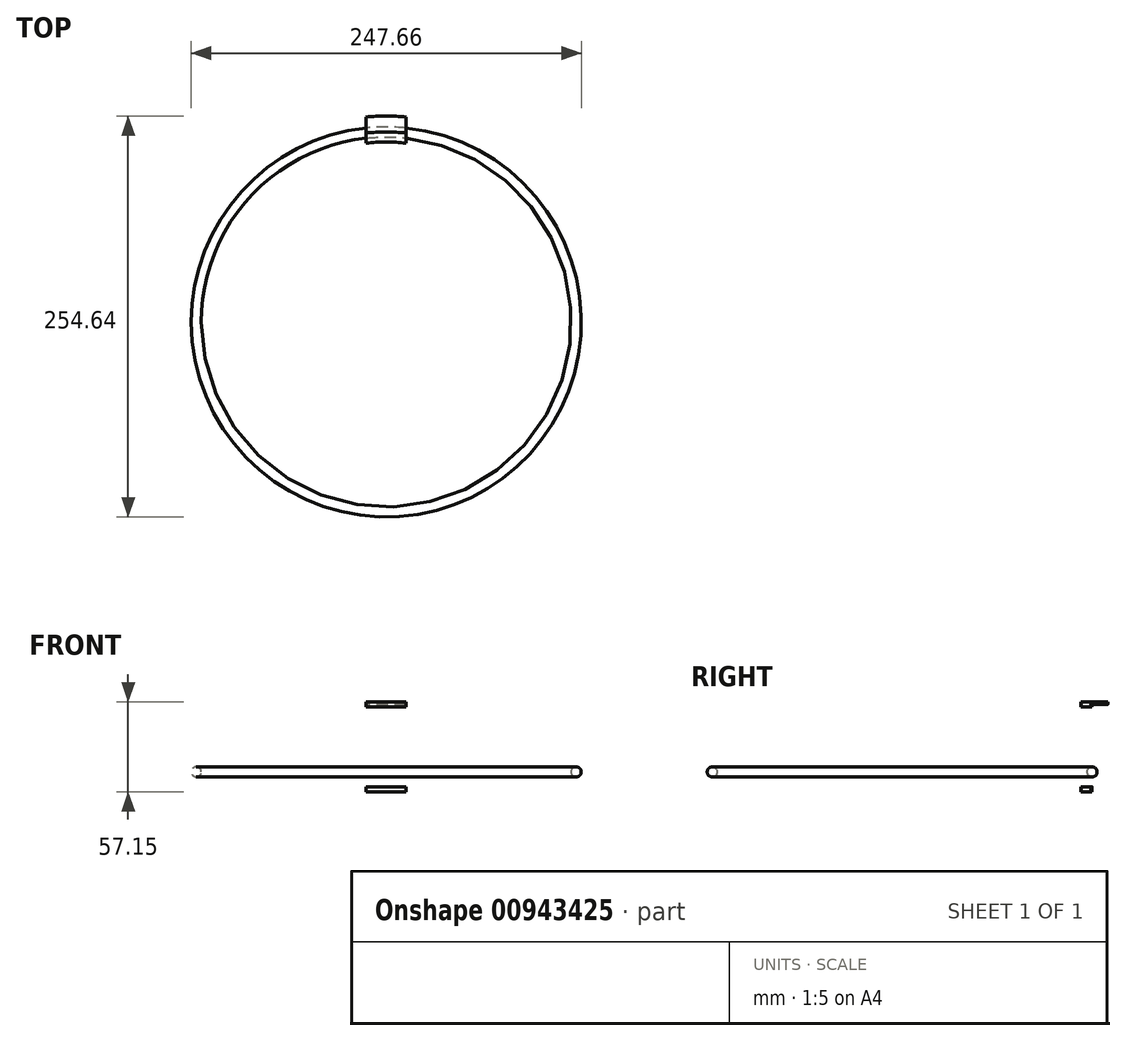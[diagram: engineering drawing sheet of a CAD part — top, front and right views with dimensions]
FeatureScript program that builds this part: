
annotation { "Feature Type Name" : "Feature", "Feature Type Description" : "" }
export const myFeature = defineFeature(function(context is Context, id is Id, definition is map)
    precondition{}
    {
        {
            var Q0;
            Q0=qCreatedBy(makeId("Right.planeOp"),FACE);
            var sketch = newSketch(context, id + "F0", { "sketchPlane" : qUnion([Q0])});
            skLineSegment(sketch, "E0", {"start": v(0, -83.04) * mm, "end": v(0, 246.82) * mm});
            skLineSegment(sketch, "E1", {"start": v(-114.3, 0) * mm, "end": v(-114.3, 57.15) * mm});
            skLineSegment(sketch, "E2", {"start": v(-114.3, 57.15) * mm, "end": v(-120.65, 57.15) * mm});
            skLineSegment(sketch, "E3", {"start": v(-120.65, 57.15) * mm, "end": v(-120.65, 0) * mm});
            skLineSegment(sketch, "E4", {"start": v(-120.65, 0) * mm, "end": v(-114.3, 0) * mm});
            skCircle(sketch, "E5", {"center": v(-120.65, 44.45) * mm, "radius": 3.18 * mm});
            skCircle(sketch, "E6", {"center": v(-120.65, 12.7) * mm, "radius": 3.18 * mm});
            skLineSegment(sketch, "E7.top", {"start": v(-114.3, 53.98) * mm, "end": v(-120.65, 53.98) * mm});
            skLineSegment(sketch, "E7.left", {"start": v(-114.3, 57.15) * mm, "end": v(-114.3, 53.98) * mm});
            skLineSegment(sketch, "E7.right", {"start": v(-120.65, 57.15) * mm, "end": v(-120.65, 53.98) * mm});
            skLineSegment(sketch, "E8.bottom", {"start": v(-114.3, 0) * mm, "end": v(-120.65, 0) * mm});
            skLineSegment(sketch, "E8.top", {"start": v(-114.3, 3.18) * mm, "end": v(-120.65, 3.18) * mm});
            skLineSegment(sketch, "E8.left", {"start": v(-114.3, 0) * mm, "end": v(-114.3, 3.18) * mm});
            skLineSegment(sketch, "E8.right", {"start": v(-120.65, 0) * mm, "end": v(-120.65, 3.18) * mm});
            skSolve(sketch);
        }
        {
            var Q0;
            Q0=makeQuery(id+"F0.imprint","IMPRINT",FACE,{"disambiguationData":[TD([[makeQuery(id+"F0.imprint","IMPRINT",EDGE,{"derivedFrom":sQuery(id+"F0.wireOp",EDGE,"E1")}),1.0]])]});
            var Q1;
            Q1=sQuery(id+"F0.wireOp",EDGE,"E0");
            revolve(context, id + "F1", {"surfaceOperationType" : NewSurfaceOperationType.NEW, "entities" : qUnion([Q0]), "axis" : qUnion([Q1]), "revolveType" : RevolveType.FULL});
        }
        {
            var Q0;
            Q0=qCreatedBy(makeId("Right.planeOp"),FACE);
            var sketch = newSketch(context, id + "F2", { "sketchPlane" : qUnion([Q0])});
            skLineSegment(sketch, "E9", {"start": v(0, 37.9) * mm, "end": v(0, -20.13) * mm});
            skLineSegment(sketch, "E10", {"start": v(120.65, 0) * mm, "end": v(120.65, 57.15) * mm});
            skLineSegment(sketch, "E11", {"start": v(120.65, 57.15) * mm, "end": v(130.8, 57.15) * mm});
            skLineSegment(sketch, "E12", {"start": v(130.8, 57.15) * mm, "end": v(130.8, 0) * mm});
            skLineSegment(sketch, "E13", {"start": v(130.8, 0) * mm, "end": v(120.65, 0) * mm});
            skCircle(sketch, "E14", {"center": v(120.65, 44.45) * mm, "radius": 3.18 * mm});
            skCircle(sketch, "E15", {"center": v(120.65, 12.7) * mm, "radius": 3.18 * mm});
            skLineSegment(sketch, "E16.top", {"start": v(120.65, 55.56) * mm, "end": v(130.8, 55.56) * mm});
            skLineSegment(sketch, "E16.left", {"start": v(120.65, 57.15) * mm, "end": v(120.65, 55.56) * mm});
            skLineSegment(sketch, "E16.right", {"start": v(130.8, 57.15) * mm, "end": v(130.8, 55.56) * mm});
            skSolve(sketch);
        }
        {
            var Q0;
            Q0=makeQuery(id+"F2.imprint","IMPRINT",FACE,{"disambiguationData":[TD([[makeQuery(id+"F2.imprint","IMPRINT",EDGE,{"derivedFrom":sQuery(id+"F2.wireOp",EDGE,"E12")}),-1.0]])]});
            var Q1;
            Q1=sQuery(id+"F2.wireOp",EDGE,"E9");
            revolve(context, id + "F3", {"surfaceOperationType" : NewSurfaceOperationType.NEW, "entities" : qUnion([Q0]), "axis" : qUnion([Q1]), "revolveType" : RevolveType.FULL});
        }
        {
            var Q0;
            Q0=qCreatedBy(makeId("Front.planeOp"),FACE);
            var sketch = newSketch(context, id + "F4", { "sketchPlane" : qUnion([Q0])});
            skLineSegment(sketch, "E17.bottom", {"start": v(12.7, 0) * mm, "end": v(-12.7, 0) * mm});
            skLineSegment(sketch, "E17.top", {"start": v(12.7, 76.2) * mm, "end": v(-12.7, 76.2) * mm});
            skLineSegment(sketch, "E17.left", {"start": v(12.7, 0) * mm, "end": v(12.7, 76.2) * mm});
            skLineSegment(sketch, "E17.right", {"start": v(-12.7, 0) * mm, "end": v(-12.7, 76.2) * mm});
            skPoint(sketch, "E18", {"position": v(0, 0) * mm});
            skSolve(sketch);
        }
        {
            var Q0;
            Q0=makeQuery(id+"F0.imprint","IMPRINT",FACE,{"disambiguationData":[TD([[makeQuery(id+"F0.imprint","IMPRINT",EDGE,{"derivedFrom":sQuery(id+"F0.wireOp",EDGE,"E1")}),1.0]])]});
            var Q1;
            Q1=sQuery(id+"F0.wireOp",EDGE,"E0");
            revolve(context, id + "F5", {"surfaceOperationType" : NewSurfaceOperationType.NEW, "entities" : qUnion([Q0]), "axis" : qUnion([Q1]), "revolveType" : RevolveType.FULL});
        }
        {
            var Q0;
            Q0 = qSketchRegion(id + "F4", true);
            extrude(context, id + "F6", {"entities" : qUnion([Q0]), "operationType" : NewBodyOperationType.INTERSECT, "endBound" : BoundingType.THROUGH_ALL, "oppositeDirection" : true, "depth" : 25.4 * mm, "offsetDistance" : 25.4 * mm});
        }
        {
            var Q0;
            Q0=qCreatedBy(makeId("Front.planeOp"),FACE);
            var sketch = newSketch(context, id + "F7", { "sketchPlane" : qUnion([Q0])});
            skLineSegment(sketch, "E19.bottom", {"start": v(-25.4, 22.23) * mm, "end": v(25.4, 22.23) * mm});
            skLineSegment(sketch, "E19.top", {"start": v(-25.4, 34.93) * mm, "end": v(25.4, 34.93) * mm});
            skLineSegment(sketch, "E19.left", {"start": v(-25.4, 22.23) * mm, "end": v(-25.4, 34.92) * mm});
            skLineSegment(sketch, "E19.right", {"start": v(25.4, 22.23) * mm, "end": v(25.4, 34.92) * mm});
            skPoint(sketch, "E20", {"position": v(0, 22.23) * mm});
            skPoint(sketch, "E21", {"position": v(-25.4, 28.58) * mm});
            skSolve(sketch);
        }
        {
            var Q0;
            Q0 = qSketchRegion(id + "F7", true);
            extrude(context, id + "F8", {"entities" : qUnion([Q0]), "operationType" : NewBodyOperationType.REMOVE, "endBound" : BoundingType.THROUGH_ALL, "depth" : 25.4 * mm, "offsetDistance" : 25.4 * mm});
        }
        {
            var Q0;
            {var subQ0=sQuery(id+"F0.wireOp",EDGE,"E6");var subQ1=sQuery(id+"F0.wireOp",EDGE,"E3");var subQ2=makeQuery(id+"F0.imprint","INTERSECT",VERTEX,{"disambiguationData":[OD(0.0)],"derivedFrom":[subQ1,subQ0]});Q0=makeQuery(id+"F0.imprint","IMPRINT",FACE,{"disambiguationData":[TD([[makeQuery(id+"F0.imprint","IMPRINT",EDGE,{"disambiguationData":[TD([[subQ2,-1.0]])],"derivedFrom":subQ1}),-1.0]])]});}
            var Q1;
            {var subQ0=sQuery(id+"F0.wireOp",EDGE,"E6");var subQ1=sQuery(id+"F0.wireOp",EDGE,"E3");var subQ2=makeQuery(id+"F0.imprint","INTERSECT",VERTEX,{"disambiguationData":[OD(0.0)],"derivedFrom":[subQ1,subQ0]});Q1=makeQuery(id+"F0.imprint","IMPRINT",FACE,{"disambiguationData":[TD([[makeQuery(id+"F0.imprint","IMPRINT",EDGE,{"disambiguationData":[TD([[subQ2,-1.0]])],"derivedFrom":subQ1}),1.0]])]});}
            var Q2;
            Q2=sQuery(id+"F0.wireOp",EDGE,"E0");
            revolve(context, id + "F9", {"surfaceOperationType" : NewSurfaceOperationType.NEW, "entities" : qUnion([Q0, Q1]), "axis" : qUnion([Q2]), "revolveType" : RevolveType.FULL});
        }
        {
            var Q0;
            Q0=makeQuery(id+"F5.opRevolve","SWEPT_BODY",BODY,{"disambiguationData":[OSD([sQuery(id+"F0.wireOp",EDGE,"E1"),sQuery(id+"F0.wireOp",EDGE,"E3"),sQuery(id+"F0.wireOp",EDGE,"E5"),sQuery(id+"F0.wireOp",EDGE,"E6"),sQuery(id+"F0.wireOp",EDGE,"E7.top"),sQuery(id+"F0.wireOp",EDGE,"E8.top")])]});
            deleteBodies(context, id + "F10", {"entities" : qUnion([Q0])});
        }
    });
